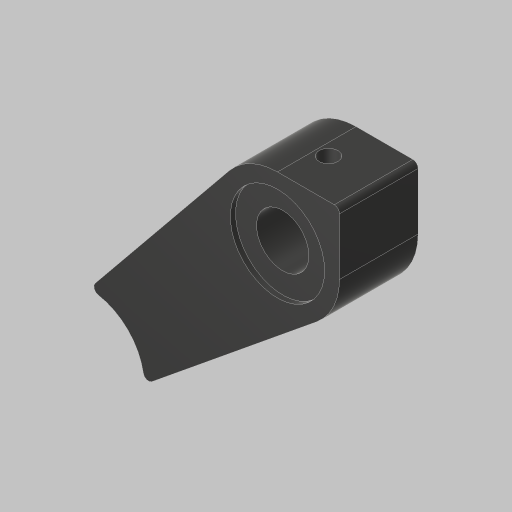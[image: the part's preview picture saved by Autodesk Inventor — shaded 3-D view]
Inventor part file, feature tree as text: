
AUTODESK INVENTOR PART (.ipt)
format: ipt  version: 2023.5 (Build 275446000, 446)  size: 169,472 bytes
history: native  units: in
note: dims shown in document units (in); Inventor stores cm internally (conversion verified against a paired STEP export)
features: sketch x4, extrude x3, fillet x1, mirror x1, plane x1, projected_geometry x1
ambient origin geometry x8: Origin, YZ Plane, XZ Plane, XY Plane, X Axis, Y Axis, Z Axis, Center Point
bodies: Solid1 (feature_tree)
feature tree (11):
  extrude  "Extrusion1"  Depth=6.0in
  fillet  "Fillet1"  Radius=1.32in
  extrude  "Extrusion2"  Depth=1.5in
  mirror  "Mirror1"
  sketch  "Sketch3"  dims[d6=0.0312in d7=0.01in]
  plane  "Work Plane1"
  extrude  "Extrusion3"  Depth=0.01in
  sketch  "Sketch1"  dims[d0=6.0in d1=6.0in d2=1.32in]
  sketch  "Sketch2"  dims[d3=0.625in d4=1.5in]
  projected_geometry  "Projected Loop1"
  sketch  "Sketch5"  dims[d8=0.01in d9=0.9375in d10=0.0in d11=0.0625in d12=1.125in d13=0.0625in d14=0.0in d15=0.24in d16=0.75in d17=1.0in d18=2.25in d19=2.25in d20=45.0deg d28=0.6in d29=0.2264in d30=0.3in d31=0.0in]
